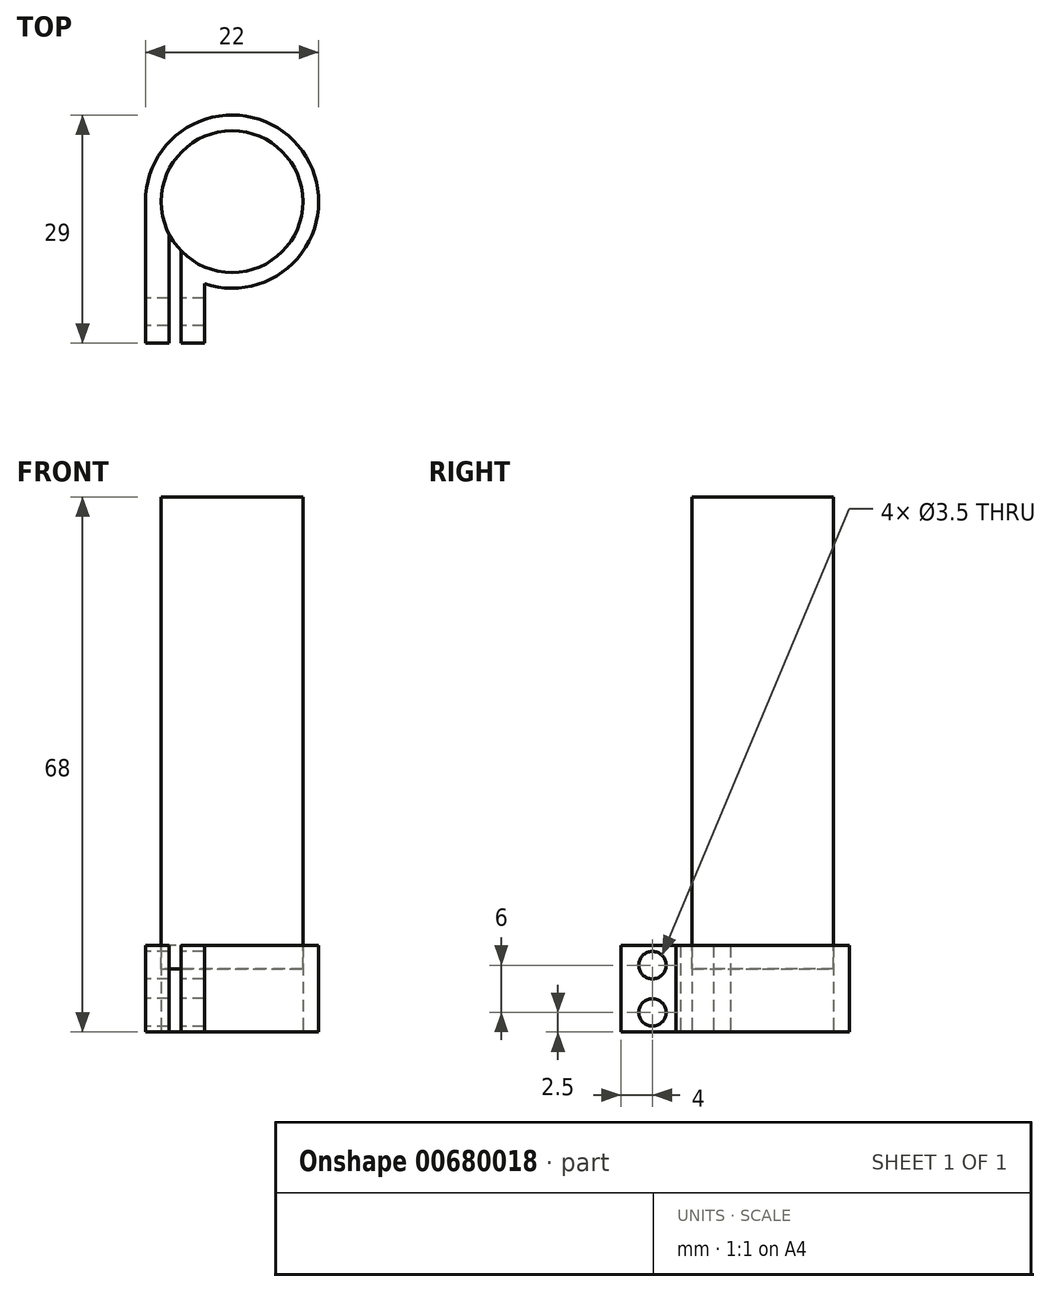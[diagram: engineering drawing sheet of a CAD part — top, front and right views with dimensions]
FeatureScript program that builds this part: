
annotation { "Feature Type Name" : "Feature", "Feature Type Description" : "" }
export const myFeature = defineFeature(function(context is Context, id is Id, definition is map)
    precondition{}
    {
        {
            var Q0;
            Q0=qCreatedBy(makeId("Front.planeOp"),FACE);
            var sketch = newSketch(context, id + "F0", { "sketchPlane" : qUnion([Q0])});
            skLineSegment(sketch, "E0", {"start": v(0, 0) * mm, "end": v(0, 8) * mm, "construction": true});
            skLineSegment(sketch, "E1", {"start": v(0, 8) * mm, "end": v(9, 8) * mm});
            skLineSegment(sketch, "E2", {"start": v(9, 8) * mm, "end": v(9, 68) * mm});
            skLineSegment(sketch, "E3", {"start": v(9, 68) * mm, "end": v(0, 68) * mm});
            skLineSegment(sketch, "E4", {"start": v(0, 68) * mm, "end": v(0, 8) * mm});
            skSolve(sketch);
        }
        {
            var Q0;
            Q0=makeQuery(id+"F0.imprint","IMPRINT",FACE,{"disambiguationData":[TD([[makeQuery(id+"F0.imprint","IMPRINT",EDGE,{"derivedFrom":sQuery(id+"F0.wireOp",EDGE,"E1")}),1.0]])]});
            var Q1;
            Q1=sQuery(id+"F0.wireOp",EDGE,"E4");
            revolve(context, id + "F1", {"entities" : qUnion([Q0]), "axis" : qUnion([Q1]), "revolveType" : RevolveType.FULL});
        }
        {
            var Q0;
            Q0=qCreatedBy(makeId("Top.planeOp"),FACE);
            var sketch = newSketch(context, id + "F2", { "sketchPlane" : qUnion([Q0])});
            skLineSegment(sketch, "E5", {"start": v(-11, -18) * mm, "end": v(-11, 0) * mm});
            skCircle(sketch, "E6", {"center": v(0, 0) * mm, "radius": 9 * mm});
            skCircle(sketch, "E7", {"center": v(0, 0) * mm, "radius": 11 * mm});
            skLineSegment(sketch, "E8", {"start": v(-11, -18) * mm, "end": v(-8, -18) * mm});
            skLineSegment(sketch, "E9", {"start": v(-8, -18) * mm, "end": v(-8, -4.12) * mm});
            skLineSegment(sketch, "E10", {"start": v(-6.5, -6.22) * mm, "end": v(-6.5, -18) * mm});
            skLineSegment(sketch, "E11", {"start": v(-6.5, -18) * mm, "end": v(-3.5, -18) * mm});
            skLineSegment(sketch, "E12", {"start": v(-3.5, -18) * mm, "end": v(-3.5, -8.3) * mm});
            skLineSegment(sketch, "E13", {"start": v(0, 0) * mm, "end": v(0, -11) * mm, "construction": true});
            skLineSegment(sketch, "E14", {"start": v(-6.5, -18) * mm, "end": v(-8, -18) * mm, "construction": true});
            skSolve(sketch);
        }
        {
            var Q0;
            {var subQ3=sQuery(id+"F2.wireOp",EDGE,"E11");Q0=makeQuery(id+"F2.imprint","IMPRINT",FACE,{"disambiguationData":[TD([[makeQuery(id+"F2.imprint","IMPRINT",EDGE,{"derivedFrom":subQ3}),1.0]])]});}
            var Q1;
            {var subQ3=sQuery(id+"F2.wireOp",EDGE,"E6");var subQ5=sQuery(id+"F2.wireOp",EDGE,"E10");var subQ7=makeQuery(id+"F2.imprint","INTERSECT",VERTEX,{"derivedFrom":[subQ3,subQ5]});Q1=makeQuery(id+"F2.imprint","IMPRINT",FACE,{"disambiguationData":[TD([[makeQuery(id+"F2.imprint","IMPRINT",EDGE,{"disambiguationData":[TD([[subQ7,-1.0]])],"derivedFrom":subQ3}),-1.0]])]});}
            var Q2;
            {var subQ3=sQuery(id+"F2.wireOp",EDGE,"E6");var subQ5=sQuery(id+"F2.wireOp",EDGE,"E9");var subQ6=makeQuery(id+"F2.imprint","INTERSECT",VERTEX,{"derivedFrom":[subQ3,subQ5]});Q2=makeQuery(id+"F2.imprint","IMPRINT",FACE,{"disambiguationData":[TD([[makeQuery(id+"F2.imprint","IMPRINT",EDGE,{"disambiguationData":[TD([[subQ6,1.0]])],"derivedFrom":subQ3}),-1.0]])]});}
            var Q3;
            {var subQ3=sQuery(id+"F2.wireOp",EDGE,"E5");Q3=makeQuery(id+"F2.imprint","IMPRINT",FACE,{"disambiguationData":[TD([[makeQuery(id+"F2.imprint","IMPRINT",EDGE,{"derivedFrom":subQ3}),-1.0]])]});}
            extrude(context, id + "F3", {"entities" : qUnion([Q0, Q1, Q2, Q3]), "depth" : 11 * mm});
        }
        {
            var Q0;
            Q0=makeQuery(id+"F3.opExtrude","SWEPT_FACE",FACE,{"disambiguationData":[OSD([sQuery(id+"F2.wireOp",EDGE,"E5")])]});
            var sketch = newSketch(context, id + "F4", { "sketchPlane" : qUnion([Q0])});
            skLineSegment(sketch, "E15.0", {"start": v(18, 11) * mm, "end": v(18, 0) * mm});
            skLineSegment(sketch, "E16", {"start": v(18, 0) * mm, "end": v(14, 0) * mm, "construction": true});
            skLineSegment(sketch, "E17", {"start": v(14, 0) * mm, "end": v(14, 2.5) * mm, "construction": true});
            skLineSegment(sketch, "E18", {"start": v(14, 2.5) * mm, "end": v(14, 8.5) * mm, "construction": true});
            skCircle(sketch, "E19", {"center": v(14, 8.5) * mm, "radius": 1.75 * mm});
            skCircle(sketch, "E20", {"center": v(14, 2.5) * mm, "radius": 1.75 * mm});
            skSolve(sketch);
        }
        {
            var Q0;
            Q0=qSketchRegion(id+"F4",true);
            extrude(context, id + "F5", {"entities" : qUnion([Q0]), "operationType" : NewBodyOperationType.REMOVE, "oppositeDirection" : true, "depth" : 25 * mm});
        }
    });
